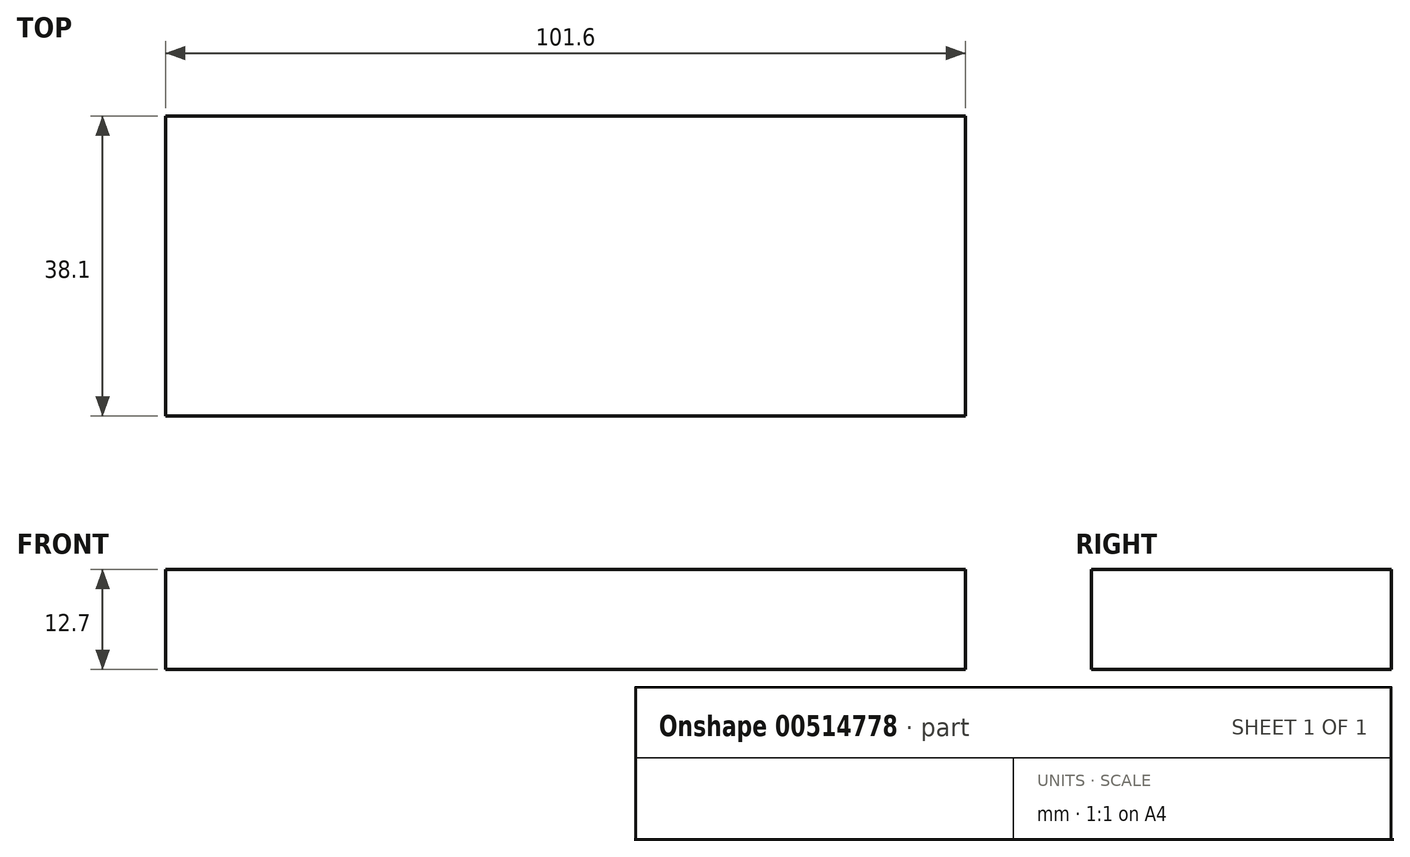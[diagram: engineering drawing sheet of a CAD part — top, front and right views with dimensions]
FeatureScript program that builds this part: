
annotation { "Feature Type Name" : "Feature", "Feature Type Description" : "" }
export const myFeature = defineFeature(function(context is Context, id is Id, definition is map)
    precondition{}
    {
        {
            var Q0;
            Q0=qCreatedBy(makeId("Top.planeOp"),FACE);
            var sketch = newSketch(context, id + "F0", { "sketchPlane" : qUnion([Q0])});
            skLineSegment(sketch, "E0.bottom", {"start": v(0, 0) * mm, "end": v(101.6, 0) * mm});
            skLineSegment(sketch, "E0.top", {"start": v(0, 38.1) * mm, "end": v(101.6, 38.1) * mm});
            skLineSegment(sketch, "E0.left", {"start": v(0, 0) * mm, "end": v(0, 38.1) * mm});
            skLineSegment(sketch, "E0.right", {"start": v(101.6, 0) * mm, "end": v(101.6, 38.1) * mm});
            skSolve(sketch);
        }
        {
            var Q0;
            Q0=makeQuery(id+"F0.imprint","IMPRINT",FACE,{"disambiguationData":[TD([[makeQuery(id+"F0.imprint","IMPRINT",EDGE,{"derivedFrom":sQuery(id+"F0.wireOp",EDGE,"E0.bottom")}),1.0]])]});
            extrude(context, id + "F1", {"entities" : qUnion([Q0]), "depth" : 12.7 * mm, "offsetDistance" : 25.4 * mm});
        }
    });
